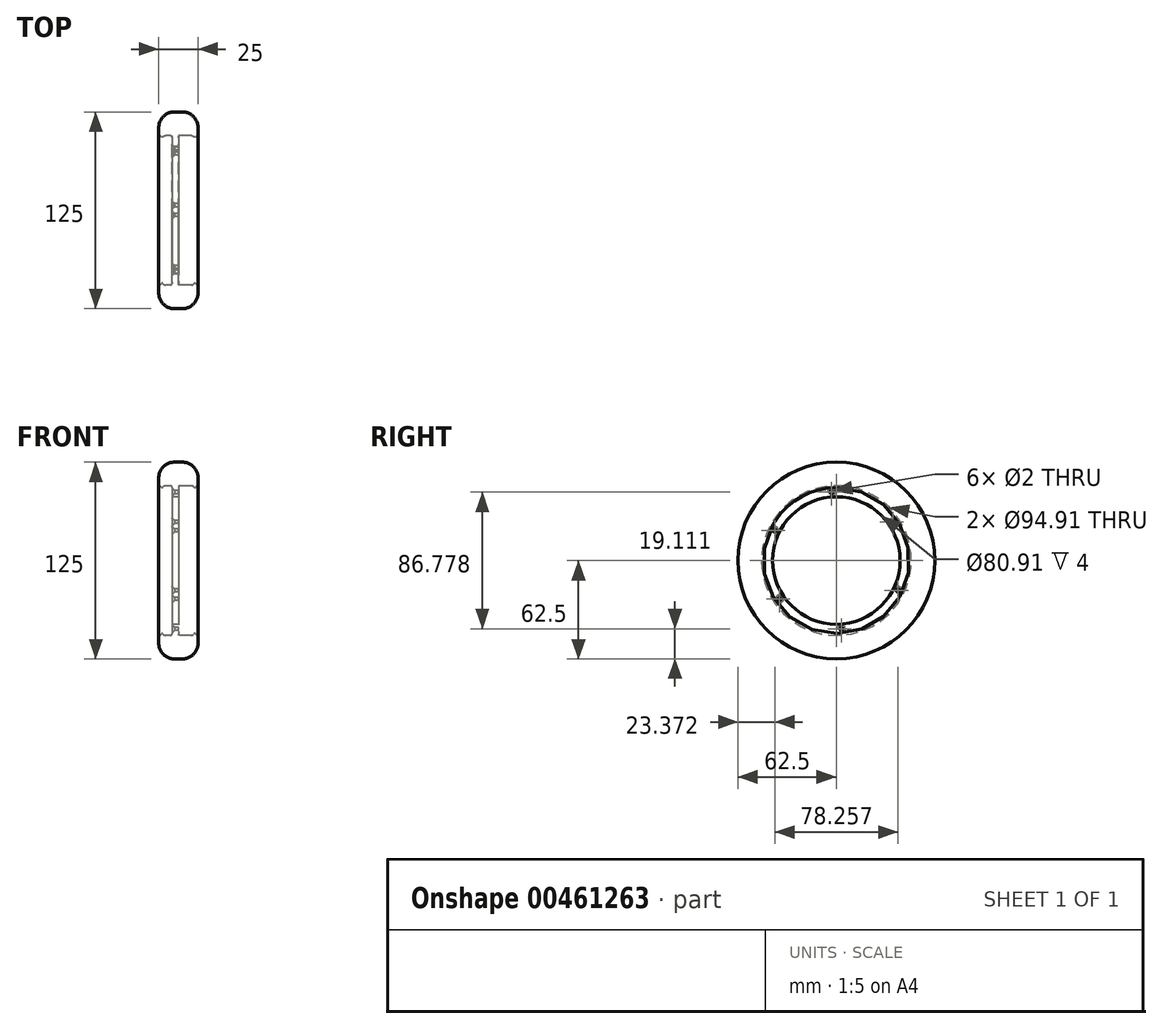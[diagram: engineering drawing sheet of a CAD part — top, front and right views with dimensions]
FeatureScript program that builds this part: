
annotation { "Feature Type Name" : "Feature", "Feature Type Description" : "" }
export const myFeature = defineFeature(function(context is Context, id is Id, definition is map)
    precondition{}
    {
        {
            var Q0;
            Q0=qCreatedBy(makeId("Front.planeOp"),FACE);
            var sketch = newSketch(context, id + "F0", { "sketchPlane" : qUnion([Q0])});
            skLineSegment(sketch, "E0.bottom", {"start": v(-2.5, 62.5) * mm, "end": v(2.5, 62.5) * mm});
            skLineSegment(sketch, "E0.left", {"start": v(-12.5, 52.5) * mm, "end": v(-12.5, 48.52) * mm});
            skLineSegment(sketch, "E0.right", {"start": v(12.5, 52.5) * mm, "end": v(12.5, 48.52) * mm});
            skPoint(sketch, "E0.middle", {"position": v(0, 0) * mm});
            skPoint(sketch, "E1.visualSharp", {"position": v(-12.5, 62.5) * mm});
            skArc(sketch, "E1.filletArc", {"start": v(-2.5, 62.5) * mm, "mid": v(-9.57, 59.57) * mm, "end": v(-12.5, 52.5) * mm});
            skPoint(sketch, "E2.visualSharp", {"position": v(12.5, 62.5) * mm});
            skArc(sketch, "E2.filletArc", {"start": v(12.5, 52.5) * mm, "mid": v(9.57, 59.57) * mm, "end": v(2.5, 62.5) * mm});
            skLineSegment(sketch, "E3", {"start": v(-12.37, 48.18) * mm, "end": v(-10.81, 46.48) * mm});
            skLineSegment(sketch, "E4", {"start": v(0, 46.96) * mm, "end": v(0, 40.46) * mm});
            skLineSegment(sketch, "E5", {"start": v(-10.1, 46.44) * mm, "end": v(-9.57, 46.93) * mm});
            skLineSegment(sketch, "E6", {"start": v(-8.22, 47.46) * mm, "end": v(-5, 47.46) * mm});
            skLineSegment(sketch, "E7.MirrorCS", {"start": v(8.22, 47.46) * mm, "end": v(0.5, 47.46) * mm});
            skLineSegment(sketch, "E8.MirrorCS", {"start": v(12.37, 48.18) * mm, "end": v(10.81, 46.48) * mm});
            skLineSegment(sketch, "E9.MirrorCS", {"start": v(10.1, 46.44) * mm, "end": v(9.57, 46.93) * mm});
            skLineSegment(sketch, "E10", {"start": v(0, 40.46) * mm, "end": v(-4, 40.46) * mm});
            skLineSegment(sketch, "E11", {"start": v(-4, 40.46) * mm, "end": v(-4, 46.46) * mm});
            skPoint(sketch, "E12.orphan", {"position": v(0, 49.92) * mm});
            skPoint(sketch, "E0.top.end.orphan", {"position": v(12.5, -62.5) * mm});
            skPoint(sketch, "E0.top.start.orphan", {"position": v(-12.5, -62.5) * mm});
            skPoint(sketch, "E13.visualSharp", {"position": v(9, 47.46) * mm});
            skArc(sketch, "E13.filletArc", {"start": v(9.57, 46.93) * mm, "mid": v(8.95, 47.32) * mm, "end": v(8.22, 47.46) * mm});
            skPoint(sketch, "E14.visualSharp", {"position": v(-9, 47.46) * mm});
            skArc(sketch, "E14.filletArc", {"start": v(-8.22, 47.46) * mm, "mid": v(-8.95, 47.32) * mm, "end": v(-9.57, 46.93) * mm});
            skPoint(sketch, "E15.visualSharp", {"position": v(-10.48, 46.1) * mm});
            skArc(sketch, "E15.filletArc", {"start": v(-10.81, 46.48) * mm, "mid": v(-10.47, 46.31) * mm, "end": v(-10.1, 46.44) * mm});
            skPoint(sketch, "E16.visualSharp", {"position": v(10.48, 46.1) * mm});
            skArc(sketch, "E16.filletArc", {"start": v(10.1, 46.44) * mm, "mid": v(10.47, 46.31) * mm, "end": v(10.81, 46.48) * mm});
            skPoint(sketch, "E17.visualSharp", {"position": v(-12.5, 48.32) * mm});
            skArc(sketch, "E17.filletArc", {"start": v(-12.5, 48.52) * mm, "mid": v(-12.47, 48.34) * mm, "end": v(-12.37, 48.18) * mm});
            skPoint(sketch, "E18.visualSharp", {"position": v(12.5, 48.32) * mm});
            skArc(sketch, "E18.filletArc", {"start": v(12.37, 48.18) * mm, "mid": v(12.47, 48.34) * mm, "end": v(12.5, 48.52) * mm});
            skPoint(sketch, "E19.orphan", {"position": v(0, 47.46) * mm});
            skPoint(sketch, "E20.visualSharp", {"position": v(-4, 47.46) * mm});
            skArc(sketch, "E20.filletArc", {"start": v(-4, 46.46) * mm, "mid": v(-4.3, 47.16) * mm, "end": v(-5, 47.46) * mm});
            skArc(sketch, "E21.filletArc", {"start": v(0.5, 47.46) * mm, "mid": v(0.15, 47.31) * mm, "end": v(0, 46.96) * mm});
            skLineSegment(sketch, "E22", {"start": v(-3.2, 0) * mm, "end": v(6.8, 0) * mm});
            skSolve(sketch);
        }
        {
            var Q0;
            Q0 = qSketchRegion(id + "F0", true);
            var Q1;
            Q1=sQuery(id+"F0.wireOp",EDGE,"E22");
            revolve(context, id + "F1", {"entities" : qUnion([Q0]), "axis" : qUnion([Q1]), "revolveType" : RevolveType.FULL});
        }
        {
            var Q0;
            Q0=makeQuery(id+"F1.opRevolve","SWEPT_FACE",FACE,{"disambiguationData":[OSD([sQuery(id+"F0.wireOp",EDGE,"E11")])]});
            var sketch = newSketch(context, id + "F2", { "sketchPlane" : qUnion([Q0])});
            skCircle(sketch, "E23.cCircle", {"center": v(0, 0) * mm, "radius": 43.5 * mm, "construction": true});
            skLineSegment(sketch, "E23.0", {"start": v(-3.1, -43.39) * mm, "end": v(-39.13, -19) * mm});
            skLineSegment(sketch, "E23.1", {"start": v(-39.13, -19) * mm, "end": v(-36.02, 24.38) * mm});
            skLineSegment(sketch, "E23.2", {"start": v(-36.02, 24.38) * mm, "end": v(3.1, 43.39) * mm});
            skLineSegment(sketch, "E23.3", {"start": v(3.1, 43.39) * mm, "end": v(39.13, 19) * mm});
            skLineSegment(sketch, "E23.4", {"start": v(39.13, 19) * mm, "end": v(36.02, -24.38) * mm});
            skLineSegment(sketch, "E23.5", {"start": v(36.02, -24.38) * mm, "end": v(-3.1, -43.39) * mm});
            skPoint(sketch, "E24", {"position": v(-3.1, -43.39) * mm});
            skPoint(sketch, "E25", {"position": v(36.02, -24.38) * mm});
            skPoint(sketch, "E26", {"position": v(-39.13, -19) * mm});
            skPoint(sketch, "E27", {"position": v(-36.02, 24.38) * mm});
            skPoint(sketch, "E28", {"position": v(39.13, 19) * mm});
            skPoint(sketch, "E29", {"position": v(3.1, 43.39) * mm});
            skSolve(sketch);
        }
        {
            var Q0;
            Q0=sQuery(id+"F2.wireOp",VERTEX,"E24");
            var Q1;
            Q1=sQuery(id+"F2.wireOp",VERTEX,"E25");
            var Q2;
            Q2=sQuery(id+"F2.wireOp",VERTEX,"E28");
            var Q3;
            Q3=sQuery(id+"F2.wireOp",VERTEX,"E29");
            var Q4;
            Q4=sQuery(id+"F2.wireOp",VERTEX,"E27");
            var Q5;
            Q5=sQuery(id+"F2.wireOp",VERTEX,"E26");
            var Q6;
            Q6=makeQuery(id+"F1.opRevolve","SWEPT_BODY",BODY,{"disambiguationData":[OSD([sQuery(id+"F0.wireOp",EDGE,"E0.bottom"),sQuery(id+"F0.wireOp",EDGE,"E0.left"),sQuery(id+"F0.wireOp",EDGE,"E0.right"),sQuery(id+"F0.wireOp",EDGE,"E1.filletArc"),sQuery(id+"F0.wireOp",EDGE,"E2.filletArc"),sQuery(id+"F0.wireOp",EDGE,"E3"),sQuery(id+"F0.wireOp",EDGE,"E4"),sQuery(id+"F0.wireOp",EDGE,"E5"),sQuery(id+"F0.wireOp",EDGE,"E6"),sQuery(id+"F0.wireOp",EDGE,"E7.MirrorCS"),sQuery(id+"F0.wireOp",EDGE,"E8.MirrorCS"),sQuery(id+"F0.wireOp",EDGE,"E9.MirrorCS"),sQuery(id+"F0.wireOp",EDGE,"E10"),sQuery(id+"F0.wireOp",EDGE,"E11"),sQuery(id+"F0.wireOp",EDGE,"E13.filletArc"),sQuery(id+"F0.wireOp",EDGE,"E14.filletArc"),sQuery(id+"F0.wireOp",EDGE,"E15.filletArc"),sQuery(id+"F0.wireOp",EDGE,"E16.filletArc"),sQuery(id+"F0.wireOp",EDGE,"E17.filletArc"),sQuery(id+"F0.wireOp",EDGE,"E18.filletArc"),sQuery(id+"F0.wireOp",EDGE,"E20.filletArc"),sQuery(id+"F0.wireOp",EDGE,"E21.filletArc")])]});
            hole(context, id + "F3", {"style" : HoleStyle.C_SINK, "endStyle" : HoleEndStyle.THROUGH, "holeDiameter" : 2 * mm, "cSinkDiameter" : 5 * mm, "cSinkAngle" : 90 * degree, "isTappedThrough" : true, "tappedDepth" : 12 * mm, "tapClearance" : 3, "locations" : qUnion([Q0, Q1, Q2, Q3, Q4, Q5]), "scope" : qUnion([Q6])});
        }
    });
